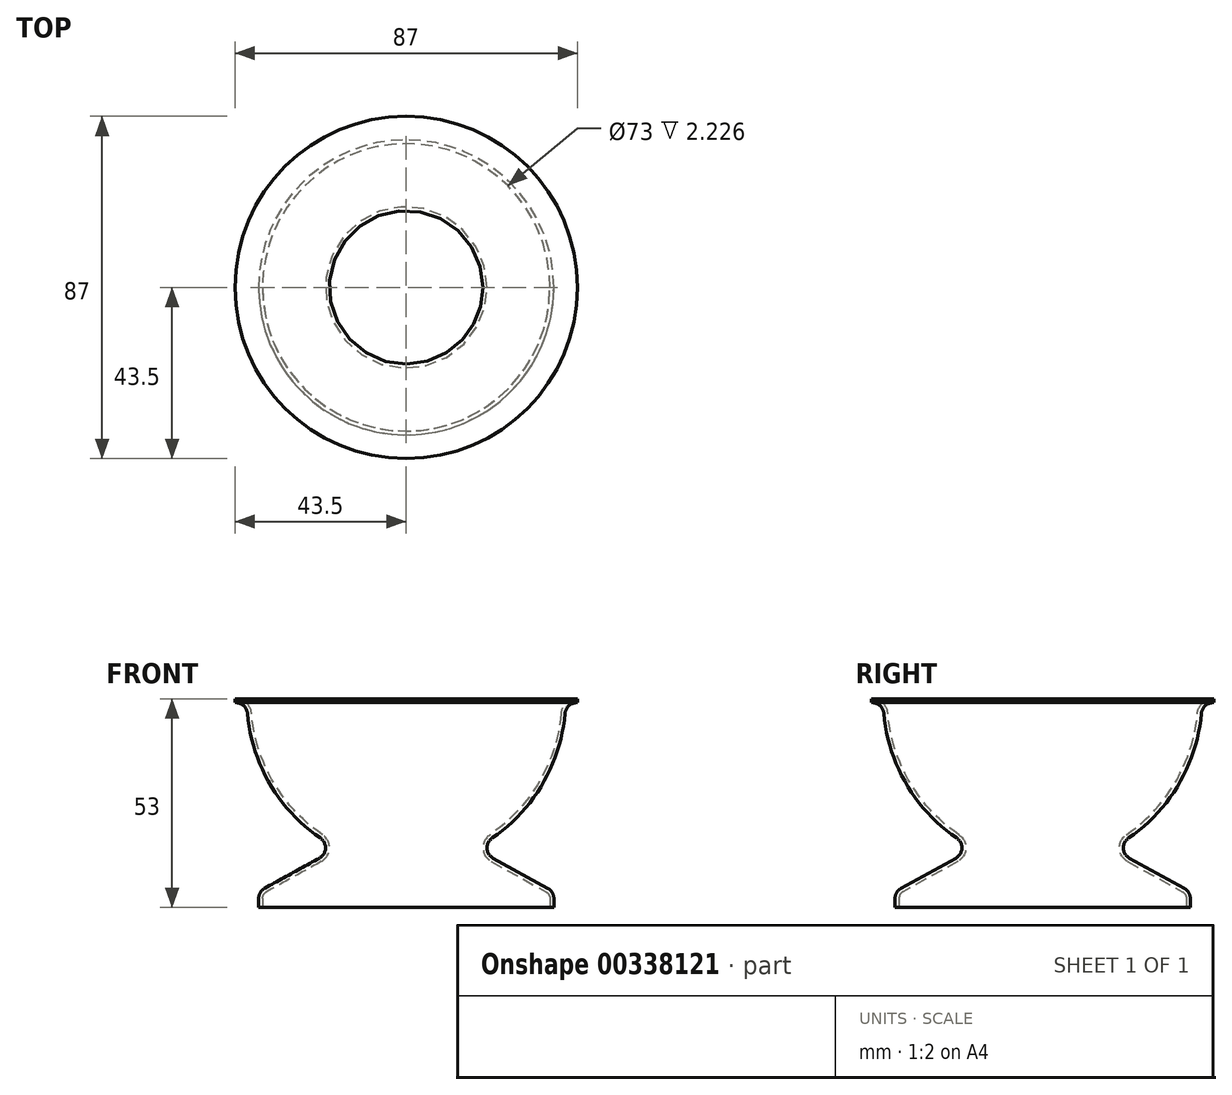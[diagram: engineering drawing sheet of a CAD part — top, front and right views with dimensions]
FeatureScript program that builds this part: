
annotation { "Feature Type Name" : "Feature", "Feature Type Description" : "" }
export const myFeature = defineFeature(function(context is Context, id is Id, definition is map)
    precondition{}
    {
        {
            var Q0;
            Q0=qCreatedBy(makeId("Front.planeOp"),FACE);
            var sketch = newSketch(context, id + "F0", { "sketchPlane" : qUnion([Q0])});
            skLineSegment(sketch, "E0", {"start": v(0, 0) * mm, "end": v(0, 19.27) * mm, "construction": true});
            skLineSegment(sketch, "E1", {"start": v(0, 0) * mm, "end": v(0, 15) * mm});
            skLineSegment(sketch, "E2", {"start": v(0, 15) * mm, "end": v(17.5, 15) * mm});
            skLineSegment(sketch, "E3", {"start": v(17.5, 15) * mm, "end": v(37.5, 4) * mm});
            skLineSegment(sketch, "E4", {"start": v(37.5, 4) * mm, "end": v(37.5, 0) * mm});
            skLineSegment(sketch, "E5", {"start": v(37.5, 0) * mm, "end": v(0, 0) * mm});
            skSolve(sketch);
        }
        {
            var Q0;
            Q0 = qSketchRegion(id + "F0", true);
            var Q1;
            Q1=sQuery(id+"F0.wireOp",EDGE,"E0");
            revolve(context, id + "F1", {"entities" : qUnion([Q0]), "axis" : qUnion([Q1]), "revolveType" : RevolveType.FULL});
        }
        {
            var Q0;
            Q0=qCreatedBy(makeId("Front.planeOp"),FACE);
            var sketch = newSketch(context, id + "F2", { "sketchPlane" : qUnion([Q0])});
            skLineSegment(sketch, "E6", {"start": v(0, 35.74) * mm, "end": v(0, -25.94) * mm, "construction": true});
            skLineSegment(sketch, "E7", {"start": v(0, 53) * mm, "end": v(40.5, 53) * mm});
            skLineSegment(sketch, "E8", {"start": v(0, 53) * mm, "end": v(0, 15) * mm});
            skLineSegment(sketch, "E9", {"start": v(0, 15) * mm, "end": v(17.5, 15) * mm});
            skArc(sketch, "E10", {"start": v(17.5, 15) * mm, "mid": v(34.3, 30.8) * mm, "end": v(40.5, 53) * mm});
            skSolve(sketch);
        }
        {
            var Q0;
            Q0=makeQuery(id+"F2.imprint","IMPRINT",FACE,{"disambiguationData":[TD([[makeQuery(id+"F2.imprint","IMPRINT",EDGE,{"derivedFrom":sQuery(id+"F2.wireOp",EDGE,"E7")}),-1.0]])]});
            var Q1;
            Q1=sQuery(id+"F2.wireOp",EDGE,"E6");
            revolve(context, id + "F3", {"operationType" : NewBodyOperationType.ADD, "entities" : qUnion([Q0]), "axis" : qUnion([Q1]), "revolveType" : RevolveType.FULL});
        }
        {
            var Q0;
            Q0=makeQuery(id+"F3.opRevolve","SWEPT_FACE",FACE,{"disambiguationData":[OSD([sQuery(id+"F2.wireOp",EDGE,"E7")])]});
            var sketch = newSketch(context, id + "F4", { "sketchPlane" : qUnion([Q0])});
            skCircle(sketch, "E11.0", {"center": v(0, 0) * mm, "radius": 43.5 * mm});
            skSolve(sketch);
        }
        {
            var Q0;
            Q0 = qSketchRegion(id + "F4", true);
            extrude(context, id + "F5", {"entities" : qUnion([Q0]), "operationType" : NewBodyOperationType.ADD, "oppositeDirection" : true, "depth" : 1 * mm});
        }
        {
            var Q0;
            Q0=makeQuery(id+"F5.boolean.opBoolean","INTERSECT",EDGE,{"derivedFrom":[makeQuery(id+"F3.opRevolve","SWEPT_FACE",FACE,{"disambiguationData":[OSD([sQuery(id+"F2.wireOp",EDGE,"E10")])]}),makeQuery(id+"F5.opExtrude","CAP_FACE",FACE,{"disambiguationData":[OSD([sQuery(id+"F4.wireOp",EDGE,"E11.0")])],"isStart":false})]});
            var Q1;
            Q1=makeQuery(id+"F3.boolean.opBoolean","MERGE",EDGE,{"derivedFrom":[makeQuery(id+"F1.opRevolve","SWEPT_EDGE",EDGE,{"disambiguationData":[OSD([sQuery(id+"F0.wireOp",EDGE,"E2"),sQuery(id+"F0.wireOp",EDGE,"E3")])]}),makeQuery(id+"F3.opRevolve","SWEPT_EDGE",EDGE,{"disambiguationData":[OSD([sQuery(id+"F2.wireOp",EDGE,"E9"),sQuery(id+"F2.wireOp",EDGE,"E10")])]})]});
            var Q2;
            Q2=makeQuery(id+"F1.opRevolve","SWEPT_EDGE",EDGE,{"disambiguationData":[OSD([sQuery(id+"F0.wireOp",EDGE,"E3"),sQuery(id+"F0.wireOp",EDGE,"E4")])]});
            fillet(context, id + "F6", {"entities" : qUnion([Q0, Q1, Q2]), "radius" : 3 * mm, "tangentPropagation" : true, "allowEdgeOverflow" : false});
        }
        {
            var Q0;
            Q0=makeQuery(id+"F5.boolean.opBoolean","MERGE",FACE,{"derivedFrom":[makeQuery(id+"F3.opRevolve","SWEPT_FACE",FACE,{"disambiguationData":[OSD([sQuery(id+"F2.wireOp",EDGE,"E7")])]}),makeQuery(id+"F5.opExtrude","CAP_FACE",FACE,{"disambiguationData":[OSD([sQuery(id+"F4.wireOp",EDGE,"E11.0")])],"isStart":true})]});
            var Q1;
            Q1=makeQuery(id+"F1.opRevolve","SWEPT_FACE",FACE,{"disambiguationData":[OSD([sQuery(id+"F0.wireOp",EDGE,"E5")])]});
            shell(context, id + "F7", {"entities" : qUnion([Q0, Q1]), "thickness" : 1 * mm});
        }
    });
